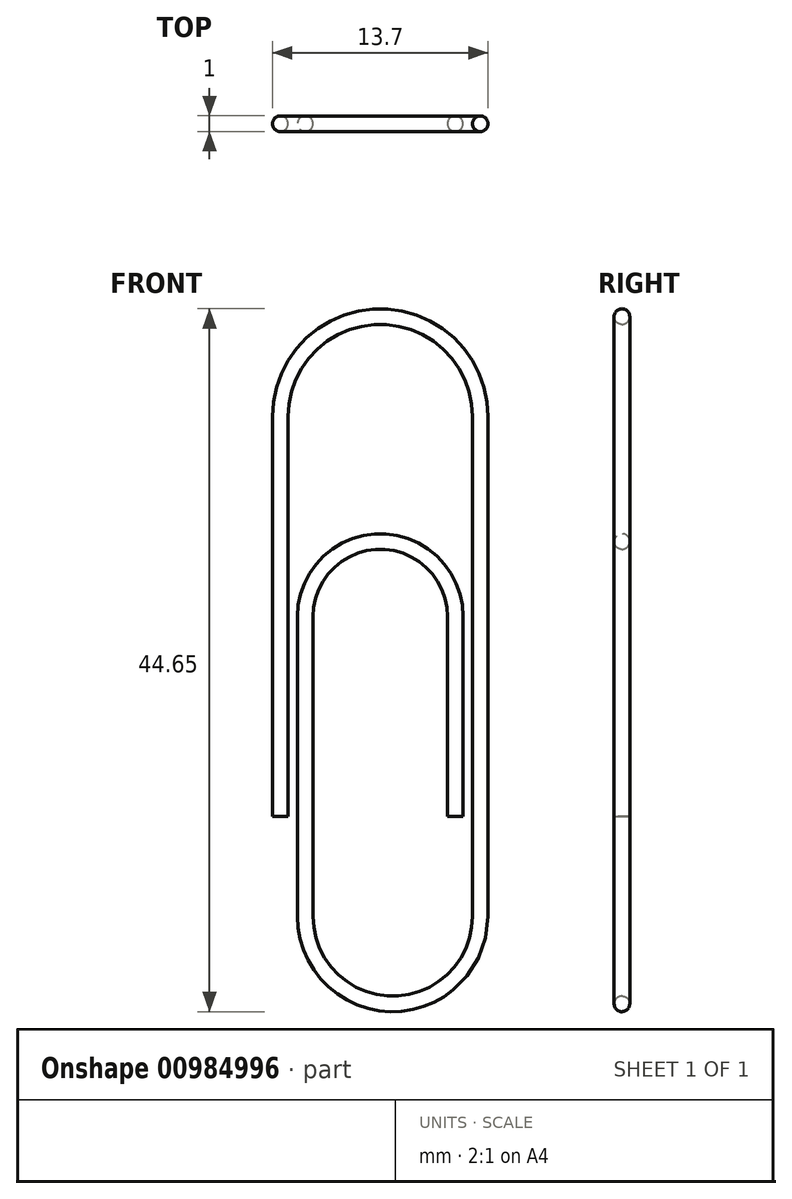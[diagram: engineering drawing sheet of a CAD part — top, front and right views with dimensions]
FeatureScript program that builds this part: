
annotation { "Feature Type Name" : "Feature", "Feature Type Description" : "" }
export const myFeature = defineFeature(function(context is Context, id is Id, definition is map)
    precondition{}
    {
        {
            var Q0;
            Q0=qCreatedBy(makeId("Front.planeOp"),FACE);
            var sketch = newSketch(context, id + "F0", { "sketchPlane" : qUnion([Q0])});
            skLineSegment(sketch, "E0", {"start": v(-6.35, 0) * mm, "end": v(-6.35, 25.4) * mm});
            skArc(sketch, "E1", {"start": v(-6.35, 25.4) * mm, "mid": v(0, 31.75) * mm, "end": v(6.35, 25.4) * mm});
            skLineSegment(sketch, "E2", {"start": v(6.35, 25.4) * mm, "end": v(6.35, -6.35) * mm});
            skArc(sketch, "E3", {"start": v(6.35, -6.35) * mm, "mid": v(0.8, -11.9) * mm, "end": v(-4.76, -6.35) * mm});
            skLineSegment(sketch, "E4", {"start": v(-4.76, -6.35) * mm, "end": v(-4.76, 12.7) * mm});
            skArc(sketch, "E5", {"start": v(-4.76, 12.7) * mm, "mid": v(0, 17.46) * mm, "end": v(4.76, 12.7) * mm});
            skLineSegment(sketch, "E6", {"start": v(4.76, 12.7) * mm, "end": v(4.76, 0) * mm});
            skPoint(sketch, "E7", {"position": v(0, 17.46) * mm});
            skSolve(sketch);
        }
        {
            var Q0;
            Q0=qCreatedBy(makeId("Top.planeOp"),FACE);
            var sketch = newSketch(context, id + "F1", { "sketchPlane" : qUnion([Q0])});
            skPoint(sketch, "E8.0", {"position": v(-6.35, 0) * mm});
            skCircle(sketch, "E9", {"center": v(-6.35, 0) * mm, "radius": 0.5 * mm});
            skSolve(sketch);
        }
        {
            var Q0;
            Q0=makeQuery(id+"F1.imprint","IMPRINT",FACE,{"disambiguationData":[TD([[makeQuery(id+"F1.imprint","IMPRINT",EDGE,{"derivedFrom":sQuery(id+"F1.wireOp",EDGE,"E9")}),1.0]])]});
            var Q1;
            Q1=sQuery(id+"F0.wireOp",EDGE,"E0");
            var Q2;
            Q2=sQuery(id+"F0.wireOp",EDGE,"E1");
            var Q3;
            Q3=sQuery(id+"F0.wireOp",EDGE,"E2");
            var Q4;
            Q4=sQuery(id+"F0.wireOp",EDGE,"E3");
            var Q5;
            Q5=sQuery(id+"F0.wireOp",EDGE,"E4");
            var Q6;
            Q6=sQuery(id+"F0.wireOp",EDGE,"E5");
            var Q7;
            Q7=sQuery(id+"F0.wireOp",EDGE,"E6");
            sweep(context, id + "F2", {"profiles" : qUnion([Q0]), "path" : qUnion([Q1, Q2, Q3, Q4, Q5, Q6, Q7])});
        }
    });
